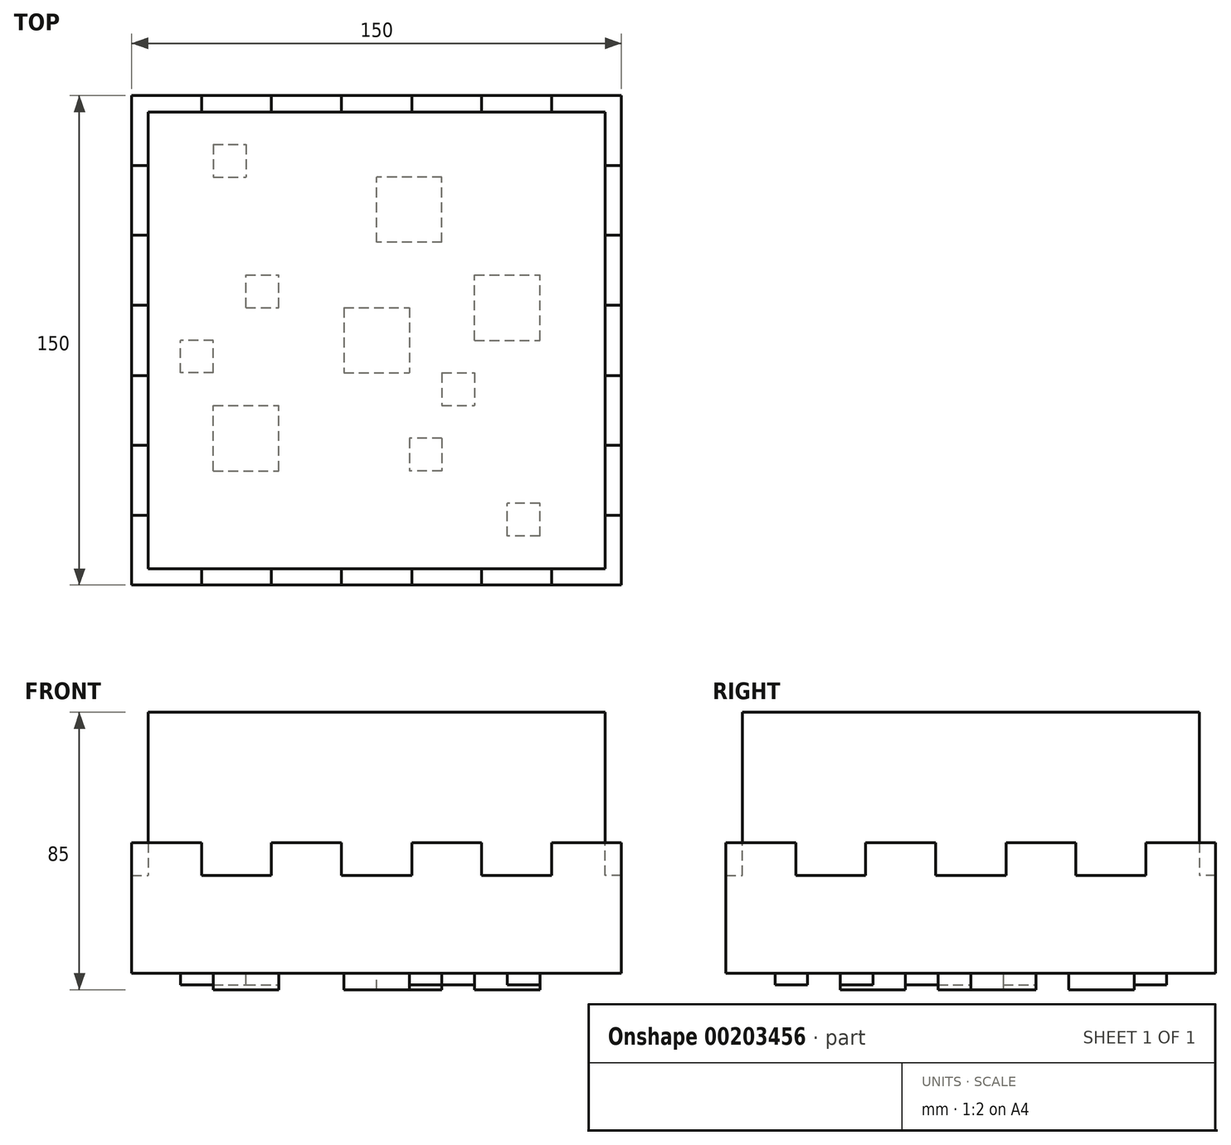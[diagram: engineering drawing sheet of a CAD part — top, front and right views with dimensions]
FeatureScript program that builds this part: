
annotation { "Feature Type Name" : "Feature", "Feature Type Description" : "" }
export const myFeature = defineFeature(function(context is Context, id is Id, definition is map)
    precondition{}
    {
        {
            var Q0;
            Q0=qCreatedBy(makeId("Top.planeOp"),FACE);
            var sketch = newSketch(context, id + "F0", { "sketchPlane" : qUnion([Q0])});
            skLineSegment(sketch, "E0.bottom", {"start": v(70, 70) * mm, "end": v(-70, 70) * mm});
            skLineSegment(sketch, "E0.top", {"start": v(70, -70) * mm, "end": v(-70, -70) * mm});
            skLineSegment(sketch, "E0.left", {"start": v(70, 70) * mm, "end": v(70, -70) * mm});
            skLineSegment(sketch, "E0.right", {"start": v(-70, 70) * mm, "end": v(-70, -70) * mm});
            skPoint(sketch, "E0.middle", {"position": v(0, 0) * mm});
            skSolve(sketch);
        }
        {
            var Q0;
            Q0=makeQuery(id+"F0.imprint","IMPRINT",FACE,{"disambiguationData":[TD([[makeQuery(id+"F0.imprint","IMPRINT",EDGE,{"derivedFrom":sQuery(id+"F0.wireOp",EDGE,"E0.bottom")}),1.0]])]});
            extrude(context, id + "F1", {"entities" : qUnion([Q0]), "endBound" : BoundingType.SYMMETRIC, "depth" : 80 * mm});
        }
        {
            var Q0;
            Q0=makeQuery(id+"F1.opExtrude","SWEPT_FACE",FACE,{"disambiguationData":[OSD([sQuery(id+"F0.wireOp",EDGE,"E0.bottom")])]});
            var sketch = newSketch(context, id + "F2", { "sketchPlane" : qUnion([Q0])});
            skLineSegment(sketch, "E1", {"start": v(70, -40) * mm, "end": v(75, -40) * mm});
            skLineSegment(sketch, "E2", {"start": v(-70, -40) * mm, "end": v(-75, -40) * mm});
            skLineSegment(sketch, "E3.bottom", {"start": v(75, -40) * mm, "end": v(-75, -40) * mm});
            skLineSegment(sketch, "E3.top", {"start": v(75, 0) * mm, "end": v(-75, 0) * mm});
            skLineSegment(sketch, "E3.left", {"start": v(75, -40) * mm, "end": v(75, 0) * mm});
            skLineSegment(sketch, "E3.right", {"start": v(-75, -40) * mm, "end": v(-75, 0) * mm});
            skLineSegment(sketch, "E4", {"start": v(75, 0) * mm, "end": v(53.6, 0) * mm, "construction": true});
            skLineSegment(sketch, "E5", {"start": v(-75, 0) * mm, "end": v(-53.6, 0) * mm, "construction": true});
            skLineSegment(sketch, "E6.bottom", {"start": v(53.6, 0) * mm, "end": v(32.2, 0) * mm});
            skLineSegment(sketch, "E6.top", {"start": v(53.6, -10) * mm, "end": v(32.2, -10) * mm});
            skLineSegment(sketch, "E6.left", {"start": v(53.6, 0) * mm, "end": v(53.6, -10) * mm});
            skLineSegment(sketch, "E6.right", {"start": v(32.2, 0) * mm, "end": v(32.2, -10) * mm});
            skLineSegment(sketch, "E7.bottom", {"start": v(-53.6, 0) * mm, "end": v(-32.2, 0) * mm});
            skLineSegment(sketch, "E7.top", {"start": v(-53.6, -10) * mm, "end": v(-32.2, -10) * mm});
            skLineSegment(sketch, "E7.left", {"start": v(-53.6, 0) * mm, "end": v(-53.6, -10) * mm});
            skLineSegment(sketch, "E7.right", {"start": v(-32.2, 0) * mm, "end": v(-32.2, -10) * mm});
            skLineSegment(sketch, "E8", {"start": v(-32.2, 0) * mm, "end": v(-10.8, 0) * mm, "construction": true});
            skLineSegment(sketch, "E9", {"start": v(32.2, 0) * mm, "end": v(10.8, 0) * mm, "construction": true});
            skLineSegment(sketch, "E10.bottom", {"start": v(10.8, 0) * mm, "end": v(-10.8, 0) * mm});
            skLineSegment(sketch, "E10.top", {"start": v(10.8, -10) * mm, "end": v(-10.8, -10) * mm});
            skLineSegment(sketch, "E10.left", {"start": v(10.8, 0) * mm, "end": v(10.8, -10) * mm});
            skLineSegment(sketch, "E10.right", {"start": v(-10.8, 0) * mm, "end": v(-10.8, -10) * mm});
            skSolve(sketch);
        }
        {
            var Q0;
            Q0=makeQuery(id+"F1.opExtrude","SWEPT_FACE",FACE,{"disambiguationData":[OSD([sQuery(id+"F0.wireOp",EDGE,"E0.right")])]});
            var sketch = newSketch(context, id + "F3", { "sketchPlane" : qUnion([Q0])});
            skLineSegment(sketch, "E11", {"start": v(70, -40) * mm, "end": v(75, -40) * mm, "construction": true});
            skLineSegment(sketch, "E12", {"start": v(-70, -40) * mm, "end": v(-75, -40) * mm, "construction": true});
            skLineSegment(sketch, "E13.bottom", {"start": v(75, -40) * mm, "end": v(-75, -40) * mm});
            skLineSegment(sketch, "E13.top", {"start": v(75, 0) * mm, "end": v(-75, 0) * mm});
            skLineSegment(sketch, "E13.left", {"start": v(75, -40) * mm, "end": v(75, 0) * mm});
            skLineSegment(sketch, "E13.right", {"start": v(-75, -40) * mm, "end": v(-75, 0) * mm});
            skLineSegment(sketch, "E14", {"start": v(75, 0) * mm, "end": v(53.6, 0) * mm, "construction": true});
            skLineSegment(sketch, "E15", {"start": v(-75, 0) * mm, "end": v(-53.6, 0) * mm, "construction": true});
            skLineSegment(sketch, "E16.bottom", {"start": v(53.6, 0) * mm, "end": v(32.2, 0) * mm});
            skLineSegment(sketch, "E16.top", {"start": v(53.6, -10) * mm, "end": v(32.2, -10) * mm});
            skLineSegment(sketch, "E16.left", {"start": v(53.6, 0) * mm, "end": v(53.6, -10) * mm});
            skLineSegment(sketch, "E16.right", {"start": v(32.2, 0) * mm, "end": v(32.2, -10) * mm});
            skLineSegment(sketch, "E17.bottom", {"start": v(-53.6, 0) * mm, "end": v(-32.2, 0) * mm});
            skLineSegment(sketch, "E17.top", {"start": v(-53.6, -10) * mm, "end": v(-32.2, -10) * mm});
            skLineSegment(sketch, "E17.left", {"start": v(-53.6, 0) * mm, "end": v(-53.6, -10) * mm});
            skLineSegment(sketch, "E17.right", {"start": v(-32.2, 0) * mm, "end": v(-32.2, -10) * mm});
            skLineSegment(sketch, "E18", {"start": v(32.2, 0) * mm, "end": v(10.8, 0) * mm, "construction": true});
            skLineSegment(sketch, "E19", {"start": v(-32.2, 0) * mm, "end": v(-10.8, 0) * mm, "construction": true});
            skLineSegment(sketch, "E20.bottom", {"start": v(10.8, 0) * mm, "end": v(-10.8, 0) * mm});
            skLineSegment(sketch, "E20.top", {"start": v(10.8, -10) * mm, "end": v(-10.8, -10) * mm});
            skLineSegment(sketch, "E20.left", {"start": v(10.8, 0) * mm, "end": v(10.8, -10) * mm});
            skLineSegment(sketch, "E20.right", {"start": v(-10.8, 0) * mm, "end": v(-10.8, -10) * mm});
            skSolve(sketch);
        }
        {
            var Q0;
            Q0=makeQuery(id+"F3.imprint","IMPRINT",FACE,{"disambiguationData":[TD([[makeQuery(id+"F3.imprint","IMPRINT",EDGE,{"derivedFrom":sQuery(id+"F3.wireOp",EDGE,"E16.top")}),1.0]])]});
            extrude(context, id + "F4", {"entities" : qUnion([Q0]), "operationType" : NewBodyOperationType.ADD, "oppositeDirection" : true, "depth" : 145 * mm});
        }
        {
            var Q0;
            Q0=makeQuery(id+"F2.imprint","IMPRINT",FACE,{"disambiguationData":[TD([[makeQuery(id+"F2.imprint","IMPRINT",EDGE,{"derivedFrom":sQuery(id+"F2.wireOp",EDGE,"E6.top")}),1.0]])]});
            extrude(context, id + "F5", {"entities" : qUnion([Q0]), "operationType" : NewBodyOperationType.ADD, "oppositeDirection" : true, "depth" : 145 * mm});
        }
        {
            var Q0;
            Q0=makeQuery(id+"F2.imprint","IMPRINT",FACE,{"disambiguationData":[TD([[makeQuery(id+"F2.imprint","IMPRINT",EDGE,{"derivedFrom":sQuery(id+"F2.wireOp",EDGE,"E6.top")}),1.0]])]});
            extrude(context, id + "F6", {"entities" : qUnion([Q0]), "operationType" : NewBodyOperationType.ADD, "depth" : 5 * mm});
        }
        {
            var Q0;
            Q0=makeQuery(id+"F3.imprint","IMPRINT",FACE,{"disambiguationData":[TD([[makeQuery(id+"F3.imprint","IMPRINT",EDGE,{"derivedFrom":sQuery(id+"F3.wireOp",EDGE,"E16.top")}),1.0]])]});
            extrude(context, id + "F7", {"entities" : qUnion([Q0]), "operationType" : NewBodyOperationType.ADD, "depth" : 5 * mm});
        }
        {
            var Q0;
            {var subQ3=sQuery(id+"F2.wireOp",EDGE,"E3.right");Q0=makeQuery(id+"F2.imprint","IMPRINT",FACE,{"disambiguationData":[TD([[makeQuery(id+"F2.imprint","IMPRINT",EDGE,{"derivedFrom":subQ3}),-1.0]])]});}
            var Q1;
            {var subQ3=sQuery(id+"F2.wireOp",EDGE,"E3.left");Q1=makeQuery(id+"F2.imprint","IMPRINT",FACE,{"disambiguationData":[TD([[makeQuery(id+"F2.imprint","IMPRINT",EDGE,{"derivedFrom":subQ3}),1.0]])]});}
            var Q2;
            Q2=makeQuery(id+"F6.opExtrude","CAP_FACE",FACE,{"disambiguationData":[OSD([sQuery(id+"F0.wireOp",EDGE,"E0.bottom"),sQuery(id+"F0.wireOp",EDGE,"E0.left"),sQuery(id+"F0.wireOp",EDGE,"E0.right"),sQuery(id+"F2.wireOp",EDGE,"E3.bottom"),sQuery(id+"F2.wireOp",EDGE,"E3.top"),sQuery(id+"F2.wireOp",EDGE,"E6.top"),sQuery(id+"F2.wireOp",EDGE,"E6.left"),sQuery(id+"F2.wireOp",EDGE,"E6.right"),sQuery(id+"F2.wireOp",EDGE,"E7.top"),sQuery(id+"F2.wireOp",EDGE,"E7.left"),sQuery(id+"F2.wireOp",EDGE,"E7.right"),sQuery(id+"F2.wireOp",EDGE,"E10.top"),sQuery(id+"F2.wireOp",EDGE,"E10.left"),sQuery(id+"F2.wireOp",EDGE,"E10.right")])],"isStart":false});
            extrude(context, id + "F8", {"entities" : qUnion([Q0, Q1]), "operationType" : NewBodyOperationType.ADD, "endBound" : BoundingType.UP_TO_SURFACE, "endBoundEntityFace" : qUnion([Q2]), "depth" : 25 * mm});
        }
        {
            var Q0;
            {var subQ1=sQuery(id+"F3.wireOp",EDGE,"E13.bottom");var subQ2=sQuery(id+"F0.wireOp",EDGE,"E0.top");var subQ3=makeQuery(id+"F1.opExtrude","SWEPT_FACE",FACE,{"disambiguationData":[OSD([subQ2])]});var subQ4=sQuery(id+"F0.wireOp",EDGE,"E0.right");var subQ8=makeQuery(id+"F4.opExtrude","SWEPT_FACE",FACE,{"disambiguationData":[OSD([subQ2,subQ4])]});Q0=makeQuery(id+"F5.boolean.opBoolean","SPLIT",FACE,{"disambiguationData":[TD([makeQuery(id+"F4.opExtrude","SWEPT_FACE",FACE,{"disambiguationData":[OSD([subQ1])]})])],"derivedFrom":makeQuery(id+"F4.boolean.opBoolean","MERGE",FACE,{"derivedFrom":[subQ3,subQ8]})});}
            var Q1;
            Q1=makeQuery(id+"F7.opExtrude","SWEPT_FACE",FACE,{"disambiguationData":[OSD([sQuery(id+"F0.wireOp",EDGE,"E0.top"),sQuery(id+"F0.wireOp",EDGE,"E0.right")])]});
            var Q2;
            Q2=makeQuery(id+"F5.opExtrude","CAP_FACE",FACE,{"disambiguationData":[OSD([sQuery(id+"F0.wireOp",EDGE,"E0.bottom"),sQuery(id+"F0.wireOp",EDGE,"E0.left"),sQuery(id+"F0.wireOp",EDGE,"E0.right"),sQuery(id+"F2.wireOp",EDGE,"E3.bottom"),sQuery(id+"F2.wireOp",EDGE,"E3.top"),sQuery(id+"F2.wireOp",EDGE,"E6.top"),sQuery(id+"F2.wireOp",EDGE,"E6.left"),sQuery(id+"F2.wireOp",EDGE,"E6.right"),sQuery(id+"F2.wireOp",EDGE,"E7.top"),sQuery(id+"F2.wireOp",EDGE,"E7.left"),sQuery(id+"F2.wireOp",EDGE,"E7.right"),sQuery(id+"F2.wireOp",EDGE,"E10.top"),sQuery(id+"F2.wireOp",EDGE,"E10.left"),sQuery(id+"F2.wireOp",EDGE,"E10.right")])],"isStart":false});
            extrude(context, id + "F9", {"entities" : qUnion([Q0, Q1]), "operationType" : NewBodyOperationType.ADD, "endBound" : BoundingType.UP_TO_SURFACE, "endBoundEntityFace" : qUnion([Q2]), "depth" : 25 * mm});
        }
        {
            var Q0;
            {var subQ0=sQuery(id+"F3.wireOp",EDGE,"E13.bottom");var subQ1=sQuery(id+"F0.wireOp",EDGE,"E0.right");var subQ2=sQuery(id+"F0.wireOp",EDGE,"E0.top");var subQ3=sQuery(id+"F2.wireOp",EDGE,"E3.bottom");var subQ4=sQuery(id+"F0.wireOp",EDGE,"E0.left");var subQ5=sQuery(id+"F0.wireOp",EDGE,"E0.bottom");Q0=makeQuery(id+"F9.boolean.opBoolean","MERGE",FACE,{"derivedFrom":[makeQuery(id+"F8.boolean.opBoolean","MERGE",FACE,{"derivedFrom":[makeQuery(id+"F7.boolean.opBoolean","MERGE",FACE,{"derivedFrom":[makeQuery(id+"F6.boolean.opBoolean","MERGE",FACE,{"derivedFrom":[makeQuery(id+"F5.boolean.opBoolean","MERGE",FACE,{"derivedFrom":[makeQuery(id+"F4.boolean.opBoolean","MERGE",FACE,{"derivedFrom":[makeQuery(id+"F1.opExtrude","CAP_FACE",FACE,{"disambiguationData":[OSD([subQ5,subQ2,subQ4,subQ1])],"isStart":true}),makeQuery(id+"F4.opExtrude","SWEPT_FACE",FACE,{"disambiguationData":[OSD([subQ0])]})]}),makeQuery(id+"F5.opExtrude","SWEPT_FACE",FACE,{"disambiguationData":[OSD([subQ3])]})]}),makeQuery(id+"F6.opExtrude","SWEPT_FACE",FACE,{"disambiguationData":[OSD([subQ3])]})]}),makeQuery(id+"F7.opExtrude","SWEPT_FACE",FACE,{"disambiguationData":[OSD([subQ0])]})]}),makeQuery(id+"F8.opExtrude","SWEPT_FACE",FACE,{"disambiguationData":[OSD([subQ3]),TDD([makeQuery(id+"F2.imprint","IMPRINT",EDGE,{"disambiguationData":[TD([[makeQuery(id+"F2.imprint","INTERSECT",VERTEX,{"derivedFrom":[makeQuery(id+"F1.opExtrude","SWEPT_EDGE",EDGE,{"disambiguationData":[OSD([subQ5,subQ1])]}),subQ3]}),1.0],[makeQuery(id+"F2.imprint","INTERSECT",VERTEX,{"derivedFrom":[subQ3,sQuery(id+"F2.wireOp",EDGE,"E3.left")]}),-1.0]])],"derivedFrom":subQ3})])]}),makeQuery(id+"F8.opExtrude","SWEPT_FACE",FACE,{"disambiguationData":[OSD([subQ3]),TDD([makeQuery(id+"F2.imprint","IMPRINT",EDGE,{"disambiguationData":[TD([[makeQuery(id+"F2.imprint","INTERSECT",VERTEX,{"derivedFrom":[makeQuery(id+"F1.opExtrude","SWEPT_EDGE",EDGE,{"disambiguationData":[OSD([subQ5,subQ4])]}),subQ3]}),-1.0],[makeQuery(id+"F2.imprint","INTERSECT",VERTEX,{"derivedFrom":[subQ3,sQuery(id+"F2.wireOp",EDGE,"E3.right")]}),1.0]])],"derivedFrom":subQ3})])]})]}),makeQuery(id+"F9.opExtrude","SWEPT_FACE",FACE,{"disambiguationData":[OSD([subQ2,subQ1,subQ0]),TDD([makeQuery(id+"F4.boolean.opBoolean","MERGE",EDGE,{"derivedFrom":[makeQuery(id+"F1.opExtrude","CAP_EDGE",EDGE,{"disambiguationData":[OSD([subQ2])],"isStart":true}),makeQuery(id+"F4.opExtrude","SWEPT_EDGE",EDGE,{"disambiguationData":[OSD([subQ2,subQ1,subQ0])]})]})])]}),makeQuery(id+"F9.opExtrude","SWEPT_FACE",FACE,{"disambiguationData":[OSD([subQ2,subQ1,subQ0]),TDD([makeQuery(id+"F7.opExtrude","SWEPT_EDGE",EDGE,{"disambiguationData":[OSD([subQ2,subQ1,subQ0])]})])]})]});}
            var sketch = newSketch(context, id + "F10", { "sketchPlane" : qUnion([Q0])});
            skLineSegment(sketch, "E21.bottom", {"start": v(-70, 70) * mm, "end": v(70, 70) * mm});
            skLineSegment(sketch, "E21.top", {"start": v(-70, -70) * mm, "end": v(70, -70) * mm});
            skLineSegment(sketch, "E21.left", {"start": v(-70, 70) * mm, "end": v(-70, -70) * mm});
            skLineSegment(sketch, "E21.right", {"start": v(70, 70) * mm, "end": v(70, -70) * mm});
            skPoint(sketch, "E21.middle", {"position": v(0, 0) * mm});
            skLineSegment(sketch, "E22", {"start": v(70, 70) * mm, "end": v(50, 70) * mm, "construction": true});
            skLineSegment(sketch, "E23", {"start": v(50, 70) * mm, "end": v(50, 60) * mm, "construction": true});
            skLineSegment(sketch, "E24.bottom", {"start": v(50, 60) * mm, "end": v(40, 60) * mm});
            skLineSegment(sketch, "E24.top", {"start": v(50, 50) * mm, "end": v(40, 50) * mm});
            skLineSegment(sketch, "E24.left", {"start": v(50, 60) * mm, "end": v(50, 50) * mm});
            skLineSegment(sketch, "E24.right", {"start": v(40, 60) * mm, "end": v(40, 50) * mm});
            skLineSegment(sketch, "E25", {"start": v(-70, -70) * mm, "end": v(-50, -70) * mm, "construction": true});
            skLineSegment(sketch, "E26", {"start": v(-50, -70) * mm, "end": v(-50, -60) * mm, "construction": true});
            skLineSegment(sketch, "E27.bottom", {"start": v(-50, -60) * mm, "end": v(-40, -60) * mm});
            skLineSegment(sketch, "E27.top", {"start": v(-50, -50) * mm, "end": v(-40, -50) * mm});
            skLineSegment(sketch, "E27.left", {"start": v(-50, -60) * mm, "end": v(-50, -50) * mm});
            skLineSegment(sketch, "E27.right", {"start": v(-40, -60) * mm, "end": v(-40, -50) * mm});
            skLineSegment(sketch, "E28", {"start": v(-70, 70) * mm, "end": v(-70, 40) * mm, "construction": true});
            skLineSegment(sketch, "E29", {"start": v(-70, 40) * mm, "end": v(-50, 40) * mm, "construction": true});
            skLineSegment(sketch, "E30.bottom", {"start": v(-50, 40) * mm, "end": v(-30, 40) * mm});
            skLineSegment(sketch, "E30.top", {"start": v(-50, 20) * mm, "end": v(-30, 20) * mm});
            skLineSegment(sketch, "E30.left", {"start": v(-50, 40) * mm, "end": v(-50, 20) * mm});
            skLineSegment(sketch, "E30.right", {"start": v(-30, 40) * mm, "end": v(-30, 20) * mm});
            skLineSegment(sketch, "E31", {"start": v(-50, 20) * mm, "end": v(-50, 10) * mm, "construction": true});
            skLineSegment(sketch, "E32.bottom", {"start": v(-50, 10) * mm, "end": v(-60, 10) * mm});
            skLineSegment(sketch, "E32.top", {"start": v(-50, 0) * mm, "end": v(-60, 0) * mm});
            skLineSegment(sketch, "E32.left", {"start": v(-50, 10) * mm, "end": v(-50, 0) * mm});
            skLineSegment(sketch, "E32.right", {"start": v(-60, 10) * mm, "end": v(-60, 0) * mm});
            skLineSegment(sketch, "E33", {"start": v(-50, 0) * mm, "end": v(-40, 0) * mm, "construction": true});
            skLineSegment(sketch, "E34", {"start": v(-40, 0) * mm, "end": v(-40, -10) * mm, "construction": true});
            skLineSegment(sketch, "E35.bottom", {"start": v(-40, -10) * mm, "end": v(-30, -10) * mm});
            skLineSegment(sketch, "E35.top", {"start": v(-40, -20) * mm, "end": v(-30, -20) * mm});
            skLineSegment(sketch, "E35.left", {"start": v(-40, -10) * mm, "end": v(-40, -20) * mm});
            skLineSegment(sketch, "E35.right", {"start": v(-30, -10) * mm, "end": v(-30, -20) * mm});
            skLineSegment(sketch, "E36", {"start": v(-30, -10) * mm, "end": v(-10, -10) * mm, "construction": true});
            skLineSegment(sketch, "E37.bottom", {"start": v(-10, -10) * mm, "end": v(10, -10) * mm});
            skLineSegment(sketch, "E37.top", {"start": v(-10, 10) * mm, "end": v(10, 10) * mm});
            skLineSegment(sketch, "E37.left", {"start": v(-10, -10) * mm, "end": v(-10, 10) * mm});
            skLineSegment(sketch, "E37.right", {"start": v(10, -10) * mm, "end": v(10, 10) * mm});
            skLineSegment(sketch, "E38", {"start": v(10, 10) * mm, "end": v(20, 10) * mm, "construction": true});
            skLineSegment(sketch, "E39.bottom", {"start": v(20, 10) * mm, "end": v(30, 10) * mm});
            skLineSegment(sketch, "E39.top", {"start": v(20, 20) * mm, "end": v(30, 20) * mm});
            skLineSegment(sketch, "E39.left", {"start": v(20, 10) * mm, "end": v(20, 20) * mm});
            skLineSegment(sketch, "E39.right", {"start": v(30, 10) * mm, "end": v(30, 20) * mm});
            skLineSegment(sketch, "E40", {"start": v(20, 20) * mm, "end": v(20, 30) * mm, "construction": true});
            skLineSegment(sketch, "E41.bottom", {"start": v(20, 30) * mm, "end": v(10, 30) * mm});
            skLineSegment(sketch, "E41.top", {"start": v(20, 40) * mm, "end": v(10, 40) * mm});
            skLineSegment(sketch, "E41.left", {"start": v(20, 30) * mm, "end": v(20, 40) * mm});
            skLineSegment(sketch, "E41.right", {"start": v(10, 30) * mm, "end": v(10, 40) * mm});
            skLineSegment(sketch, "E42", {"start": v(30, 10) * mm, "end": v(30, 0) * mm, "construction": true});
            skLineSegment(sketch, "E43.bottom", {"start": v(30, 0) * mm, "end": v(50, 0) * mm});
            skLineSegment(sketch, "E43.top", {"start": v(30, -20) * mm, "end": v(50, -20) * mm});
            skLineSegment(sketch, "E43.left", {"start": v(30, 0) * mm, "end": v(30, -20) * mm});
            skLineSegment(sketch, "E43.right", {"start": v(50, 0) * mm, "end": v(50, -20) * mm});
            skLineSegment(sketch, "E44", {"start": v(30, -20) * mm, "end": v(30, -30) * mm, "construction": true});
            skLineSegment(sketch, "E45", {"start": v(30, -30) * mm, "end": v(20, -30) * mm, "construction": true});
            skLineSegment(sketch, "E46.bottom", {"start": v(20, -30) * mm, "end": v(0, -30) * mm});
            skLineSegment(sketch, "E46.top", {"start": v(20, -50) * mm, "end": v(0, -50) * mm});
            skLineSegment(sketch, "E46.left", {"start": v(20, -30) * mm, "end": v(20, -50) * mm});
            skLineSegment(sketch, "E46.right", {"start": v(0, -30) * mm, "end": v(0, -50) * mm});
            skSolve(sketch);
        }
        {
            var Q0;
            Q0=makeQuery(id+"F10.imprint","IMPRINT",FACE,{"disambiguationData":[TD([[makeQuery(id+"F10.imprint","IMPRINT",EDGE,{"derivedFrom":sQuery(id+"F10.wireOp",EDGE,"E32.bottom")}),1.0]])]});
            var Q1;
            Q1=makeQuery(id+"F10.imprint","IMPRINT",FACE,{"disambiguationData":[TD([[makeQuery(id+"F10.imprint","IMPRINT",EDGE,{"derivedFrom":sQuery(id+"F10.wireOp",EDGE,"E35.bottom")}),-1.0]])]});
            var Q2;
            Q2=makeQuery(id+"F10.imprint","IMPRINT",FACE,{"disambiguationData":[TD([[makeQuery(id+"F10.imprint","IMPRINT",EDGE,{"derivedFrom":sQuery(id+"F10.wireOp",EDGE,"E27.bottom")}),1.0]])]});
            var Q3;
            Q3=makeQuery(id+"F10.imprint","IMPRINT",FACE,{"disambiguationData":[TD([[makeQuery(id+"F10.imprint","IMPRINT",EDGE,{"derivedFrom":sQuery(id+"F10.wireOp",EDGE,"E39.bottom")}),1.0]])]});
            var Q4;
            Q4=makeQuery(id+"F10.imprint","IMPRINT",FACE,{"disambiguationData":[TD([[makeQuery(id+"F10.imprint","IMPRINT",EDGE,{"derivedFrom":sQuery(id+"F10.wireOp",EDGE,"E41.bottom")}),-1.0]])]});
            var Q5;
            Q5=makeQuery(id+"F10.imprint","IMPRINT",FACE,{"disambiguationData":[TD([[makeQuery(id+"F10.imprint","IMPRINT",EDGE,{"derivedFrom":sQuery(id+"F10.wireOp",EDGE,"E24.bottom")}),1.0]])]});
            extrude(context, id + "F11", {"entities" : qUnion([Q0, Q1, Q2, Q3, Q4, Q5]), "operationType" : NewBodyOperationType.ADD, "depth" : 3.5 * mm});
        }
        {
            var Q0;
            Q0=makeQuery(id+"F10.imprint","IMPRINT",FACE,{"disambiguationData":[TD([[makeQuery(id+"F10.imprint","IMPRINT",EDGE,{"derivedFrom":sQuery(id+"F10.wireOp",EDGE,"E43.bottom")}),-1.0]])]});
            var Q1;
            Q1=makeQuery(id+"F10.imprint","IMPRINT",FACE,{"disambiguationData":[TD([[makeQuery(id+"F10.imprint","IMPRINT",EDGE,{"derivedFrom":sQuery(id+"F10.wireOp",EDGE,"E37.bottom")}),1.0]])]});
            var Q2;
            Q2=makeQuery(id+"F10.imprint","IMPRINT",FACE,{"disambiguationData":[TD([[makeQuery(id+"F10.imprint","IMPRINT",EDGE,{"derivedFrom":sQuery(id+"F10.wireOp",EDGE,"E30.bottom")}),-1.0]])]});
            var Q3;
            Q3=makeQuery(id+"F10.imprint","IMPRINT",FACE,{"disambiguationData":[TD([[makeQuery(id+"F10.imprint","IMPRINT",EDGE,{"derivedFrom":sQuery(id+"F10.wireOp",EDGE,"E46.bottom")}),1.0]])]});
            extrude(context, id + "F12", {"entities" : qUnion([Q0, Q1, Q2, Q3]), "operationType" : NewBodyOperationType.ADD, "depth" : 5 * mm});
        }
    });
